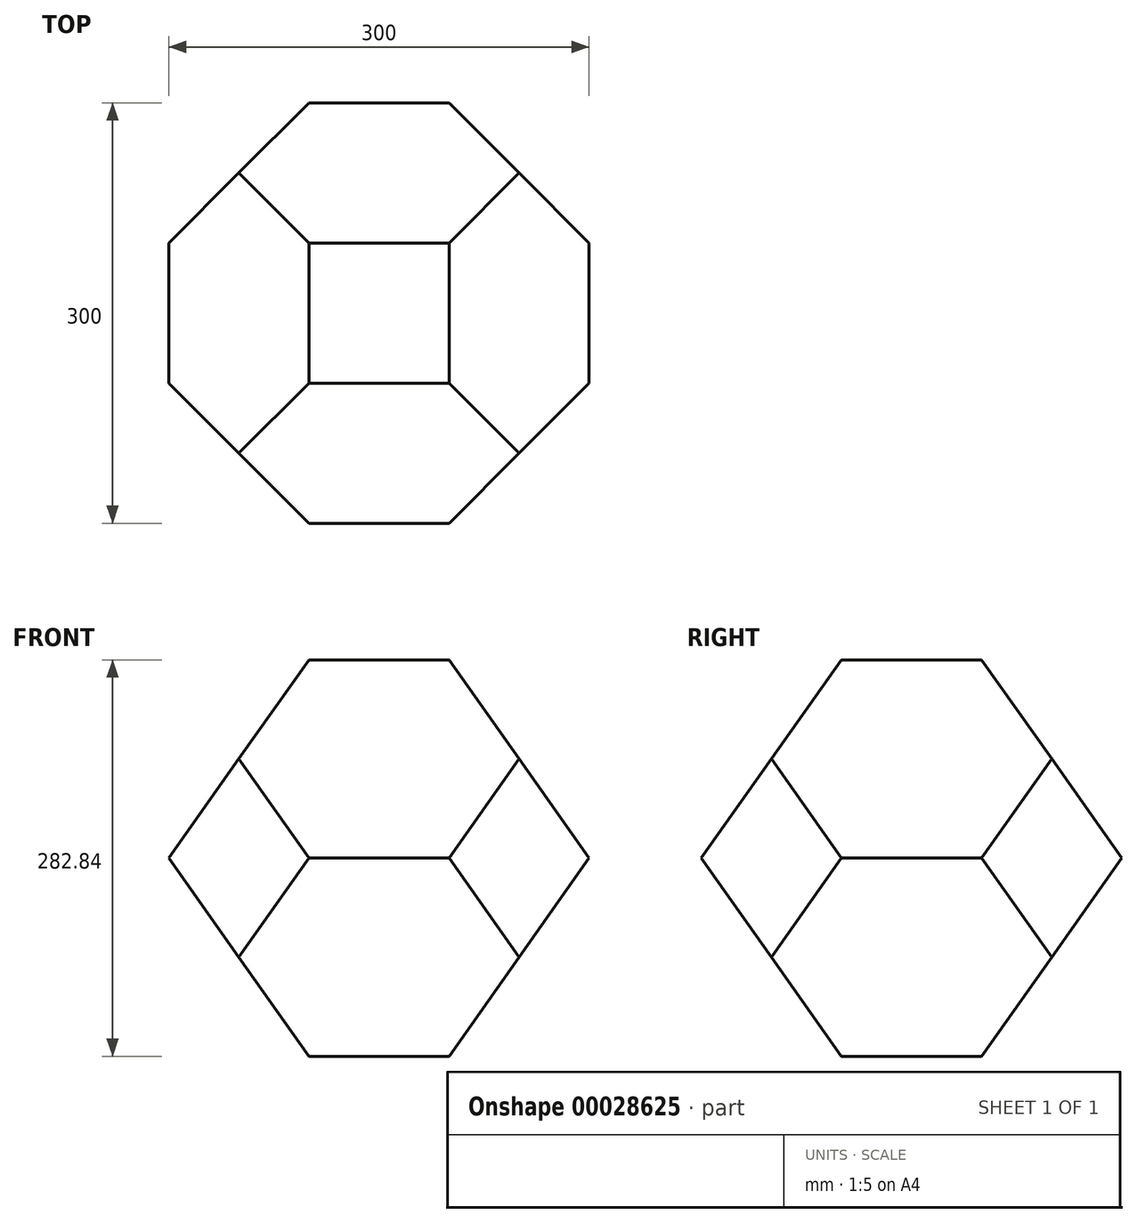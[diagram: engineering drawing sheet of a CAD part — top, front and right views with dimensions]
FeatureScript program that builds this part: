
annotation { "Feature Type Name" : "Feature", "Feature Type Description" : "" }
export const myFeature = defineFeature(function(context is Context, id is Id, definition is map)
    precondition{}
    {
        {
            var Q0;
            Q0=qCreatedBy(makeId("Top.planeOp"),FACE);
            var sketch = newSketch(context, id + "F0", { "sketchPlane" : qUnion([Q0])});
            skCircle(sketch, "E0", {"center": v(0, 0) * mm, "radius": 212.13 * mm});
            skLineSegment(sketch, "E1", {"start": v(-150, -150) * mm, "end": v(150, 150) * mm, "construction": true});
            skLineSegment(sketch, "E2.bottom", {"start": v(-150, -150) * mm, "end": v(150, -150) * mm});
            skLineSegment(sketch, "E2.top", {"start": v(-150, 150) * mm, "end": v(150, 150) * mm});
            skLineSegment(sketch, "E2.left", {"start": v(-150, -150) * mm, "end": v(-150, 150) * mm});
            skLineSegment(sketch, "E2.right", {"start": v(150, -150) * mm, "end": v(150, 150) * mm});
            skSolve(sketch);
        }
        {
            var Q0;
            Q0=qCreatedBy(makeId("Right.planeOp"),FACE);
            var sketch = newSketch(context, id + "F1", { "sketchPlane" : qUnion([Q0])});
            skLineSegment(sketch, "E3", {"start": v(-150, 0) * mm, "end": v(150, 0) * mm});
            skLineSegment(sketch, "E4", {"start": v(150, 0) * mm, "end": v(0, 212.13) * mm});
            skLineSegment(sketch, "E5", {"start": v(0, 212.13) * mm, "end": v(-150, 0) * mm});
            skSolve(sketch);
        }
        {
            var Q0;
            Q0=makeQuery(id+"F1.imprint","IMPRINT",FACE,{"disambiguationData":[TD([[makeQuery(id+"F1.imprint","IMPRINT",EDGE,{"derivedFrom":sQuery(id+"F1.wireOp",EDGE,"E3")}),1.0]])]});
            extrude(context, id + "F2", {"entities" : qUnion([Q0]), "depth" : 150 * mm, "hasSecondDirection" : true, "secondDirectionOppositeDirection" : true, "secondDirectionDepth" : 150 * mm});
        }
        {
            var Q0;
            Q0=qCreatedBy(makeId("Front.planeOp"),FACE);
            var sketch = newSketch(context, id + "F3", { "sketchPlane" : qUnion([Q0])});
            skLineSegment(sketch, "E6", {"start": v(0, 0) * mm, "end": v(0, -178.5) * mm});
            skSolve(sketch);
        }
        {
            var Q0;
            Q0=makeQuery(id+"F2.opExtrude","SWEPT_BODY",BODY,{"disambiguationData":[OSD([sQuery(id+"F1.wireOp",EDGE,"E3"),sQuery(id+"F1.wireOp",EDGE,"E4"),sQuery(id+"F1.wireOp",EDGE,"E5")])]});
            var Q1;
            Q1=sQuery(id+"F3.wireOp",EDGE,"E6");
            transform(context, id + "F4", {"entities" : qUnion([Q0]), "transformType" : TransformType.ROTATION, "transformAxis" : qUnion([Q1]), "angle" : 90 * degree, "makeCopy" : true});
        }
        {
            var Q0;
            Q0=makeQuery(id+"F2.opExtrude","SWEPT_BODY",BODY,{"disambiguationData":[OSD([sQuery(id+"F1.wireOp",EDGE,"E3"),sQuery(id+"F1.wireOp",EDGE,"E4"),sQuery(id+"F1.wireOp",EDGE,"E5")])]});
            var Q1;
            Q1=makeQuery(id+"F4.opPattern","COPY",BODY,{"derivedFrom":makeQuery(id+"F2.opExtrude","SWEPT_BODY",BODY,{"disambiguationData":[OSD([sQuery(id+"F1.wireOp",EDGE,"E3"),sQuery(id+"F1.wireOp",EDGE,"E4"),sQuery(id+"F1.wireOp",EDGE,"E5")])]}),"instanceName":"1"});
            booleanBodies(context, id + "F5", {"operationType" : BooleanOperationType.INTERSECTION, "tools" : qUnion([Q0, Q1])});
        }
        {
            var Q0;
            {var subQ0=makeQuery(id+"F2.opExtrude","SWEPT_BODY",BODY,{"disambiguationData":[OSD([sQuery(id+"F1.wireOp",EDGE,"E3"),sQuery(id+"F1.wireOp",EDGE,"E4"),sQuery(id+"F1.wireOp",EDGE,"E5")])]});Q0=makeQuery(id+"F5.opBoolean","INTERSECT",BODY,{"derivedFrom":[subQ0,makeQuery(id+"F4.opPattern","COPY",BODY,{"derivedFrom":subQ0,"instanceName":"1"})]});}
            var Q1;
            Q1=sQuery(id+"F0.wireOp",EDGE,"E1");
            transform(context, id + "F6", {"entities" : qUnion([Q0]), "transformType" : TransformType.ROTATION, "transformAxis" : qUnion([Q1]), "angle" : 180 * degree, "makeCopy" : true});
        }
        {
            var Q0;
            {var subQ0=makeQuery(id+"F2.opExtrude","SWEPT_BODY",BODY,{"disambiguationData":[OSD([sQuery(id+"F1.wireOp",EDGE,"E3"),sQuery(id+"F1.wireOp",EDGE,"E4"),sQuery(id+"F1.wireOp",EDGE,"E5")])]});Q0=makeQuery(id+"F5.opBoolean","INTERSECT",BODY,{"derivedFrom":[subQ0,makeQuery(id+"F4.opPattern","COPY",BODY,{"derivedFrom":subQ0,"instanceName":"1"})]});}
            var Q1;
            {var subQ0=makeQuery(id+"F2.opExtrude","SWEPT_BODY",BODY,{"disambiguationData":[OSD([sQuery(id+"F1.wireOp",EDGE,"E3"),sQuery(id+"F1.wireOp",EDGE,"E4"),sQuery(id+"F1.wireOp",EDGE,"E5")])]});Q1=makeQuery(id+"F6.opPattern","COPY",BODY,{"derivedFrom":makeQuery(id+"F5.opBoolean","INTERSECT",BODY,{"derivedFrom":[subQ0,makeQuery(id+"F4.opPattern","COPY",BODY,{"derivedFrom":subQ0,"instanceName":"1"})]}),"instanceName":"1"});}
            booleanBodies(context, id + "F7", {"operationType" : BooleanOperationType.UNION, "tools" : qUnion([Q0, Q1])});
        }
        {
            var Q0;
            {var subQ0=makeQuery(id+"F2.opExtrude","SWEPT_FACE",FACE,{"disambiguationData":[OSD([sQuery(id+"F1.wireOp",EDGE,"E4")])]});var subQ1=makeQuery(id+"F2.opExtrude","SWEPT_FACE",FACE,{"disambiguationData":[OSD([sQuery(id+"F1.wireOp",EDGE,"E5")])]});Q0=makeQuery(id+"F5.opBoolean","INTERSECT",VERTEX,{"derivedFrom":[subQ0,subQ1,makeQuery(id+"F4.opPattern","COPY",FACE,{"derivedFrom":subQ0,"instanceName":"1"}),makeQuery(id+"F4.opPattern","COPY",FACE,{"derivedFrom":subQ1,"instanceName":"1"})]});}
            var Q1;
            {var subQ0=sQuery(id+"F1.wireOp",EDGE,"E3");var subQ1=sQuery(id+"F1.wireOp",EDGE,"E5");var subQ2=makeQuery(id+"F5.opBoolean","MERGE",VERTEX,{"derivedFrom":[makeQuery(id+"F2.opExtrude","CAP_VERTEX",VERTEX,{"disambiguationData":[OSD([subQ0,subQ1])],"isStart":true}),makeQuery(id+"F4.opPattern","COPY",VERTEX,{"derivedFrom":makeQuery(id+"F2.opExtrude","CAP_VERTEX",VERTEX,{"disambiguationData":[OSD([subQ0,subQ1])],"isStart":false}),"instanceName":"1"})]});Q1=makeQuery(id+"F7.opBoolean","MERGE",VERTEX,{"derivedFrom":[subQ2,makeQuery(id+"F6.opPattern","COPY",VERTEX,{"derivedFrom":subQ2,"instanceName":"1"})]});}
            var Q2;
            {var subQ0=makeQuery(id+"F2.opExtrude","SWEPT_FACE",FACE,{"disambiguationData":[OSD([sQuery(id+"F1.wireOp",EDGE,"E4")])]});var subQ1=makeQuery(id+"F2.opExtrude","SWEPT_FACE",FACE,{"disambiguationData":[OSD([sQuery(id+"F1.wireOp",EDGE,"E5")])]});Q2=makeQuery(id+"F6.opPattern","COPY",VERTEX,{"derivedFrom":makeQuery(id+"F5.opBoolean","INTERSECT",VERTEX,{"derivedFrom":[subQ0,subQ1,makeQuery(id+"F4.opPattern","COPY",FACE,{"derivedFrom":subQ0,"instanceName":"1"}),makeQuery(id+"F4.opPattern","COPY",FACE,{"derivedFrom":subQ1,"instanceName":"1"})]}),"instanceName":"1"});}
            cPlane(context, id + "F8", {"entities" : qUnion([Q0, Q1, Q2]), "cplaneType" : CPlaneType.THREE_POINT, "offset" : 150 * mm, "width" : 150 * mm, "height" : 150 * mm});
        }
        {
            var Q0;
            Q0=qCreatedBy(id+"F8.planeOp",FACE);
            var sketch = newSketch(context, id + "F9", { "sketchPlane" : qUnion([Q0])});
            skLineSegment(sketch, "E7.0", {"start": v(0, 212.13) * mm, "end": v(212.13, 0) * mm, "construction": true});
            skLineSegment(sketch, "E8", {"start": v(0, 212.13) * mm, "end": v(70.71, 141.42) * mm, "construction": true});
            skLineSegment(sketch, "E9.bottom", {"start": v(132.6, 346.11) * mm, "end": v(-117.64, 346.11) * mm});
            skLineSegment(sketch, "E9.top", {"start": v(132.6, 141.42) * mm, "end": v(-117.64, 141.42) * mm});
            skLineSegment(sketch, "E9.left", {"start": v(132.6, 346.11) * mm, "end": v(132.6, 141.42) * mm});
            skLineSegment(sketch, "E9.right", {"start": v(-117.64, 346.11) * mm, "end": v(-117.64, 141.42) * mm});
            skSolve(sketch);
        }
        {
            var Q0;
            Q0=qCreatedBy(id+"F8.planeOp",FACE);
            var sketch = newSketch(context, id + "F10", { "sketchPlane" : qUnion([Q0])});
            skLineSegment(sketch, "E10", {"start": v(0, 0) * mm, "end": v(-470.52, 0) * mm});
            skLineSegment(sketch, "E11", {"start": v(0, 0) * mm, "end": v(0, -398.6) * mm});
            skSolve(sketch);
        }
        {
            var Q0;
            Q0=makeQuery(id+"F9.imprint","IMPRINT",FACE,{"disambiguationData":[TD([[makeQuery(id+"F9.imprint","IMPRINT",EDGE,{"derivedFrom":sQuery(id+"F9.wireOp",EDGE,"E9.bottom")}),1.0]])]});
            extrude(context, id + "F11", {"entities" : qUnion([Q0]), "depth" : 80 * mm, "hasSecondDirection" : true, "secondDirectionOppositeDirection" : true, "secondDirectionDepth" : 80 * mm});
        }
        {
            var Q0;
            Q0=makeQuery(id+"F11.opExtrude","SWEPT_BODY",BODY,{"disambiguationData":[OSD([sQuery(id+"F9.wireOp",EDGE,"E9.bottom"),sQuery(id+"F9.wireOp",EDGE,"E9.top"),sQuery(id+"F9.wireOp",EDGE,"E9.left"),sQuery(id+"F9.wireOp",EDGE,"E9.right")])]});
            var Q1;
            Q1=sQuery(id+"F10.wireOp",EDGE,"E10");
            circularPattern(context, id + "F12", {"entities" : qUnion([Q0]), "axis" : qUnion([Q1]), "angle" : 90 * degree, "instanceCount" : 4});
        }
        {
            var Q0;
            Q0=makeQuery(id+"F12.opPattern","COPY",BODY,{"derivedFrom":makeQuery(id+"F11.opExtrude","SWEPT_BODY",BODY,{"disambiguationData":[OSD([sQuery(id+"F9.wireOp",EDGE,"E9.bottom"),sQuery(id+"F9.wireOp",EDGE,"E9.top"),sQuery(id+"F9.wireOp",EDGE,"E9.left"),sQuery(id+"F9.wireOp",EDGE,"E9.right")])]}),"instanceName":"3"});
            var Q1;
            Q1=makeQuery(id+"F12.opPattern","COPY",BODY,{"derivedFrom":makeQuery(id+"F11.opExtrude","SWEPT_BODY",BODY,{"disambiguationData":[OSD([sQuery(id+"F9.wireOp",EDGE,"E9.bottom"),sQuery(id+"F9.wireOp",EDGE,"E9.top"),sQuery(id+"F9.wireOp",EDGE,"E9.left"),sQuery(id+"F9.wireOp",EDGE,"E9.right")])]}),"instanceName":"1"});
            var Q2;
            Q2=sQuery(id+"F10.wireOp",EDGE,"E11");
            circularPattern(context, id + "F13", {"entities" : qUnion([Q0, Q1]), "axis" : qUnion([Q2]), "angle" : 90 * degree, "instanceCount" : 2});
        }
        {
            var Q0;
            Q0=makeQuery(id+"F11.opExtrude","SWEPT_BODY",BODY,{"disambiguationData":[OSD([sQuery(id+"F9.wireOp",EDGE,"E9.bottom"),sQuery(id+"F9.wireOp",EDGE,"E9.top"),sQuery(id+"F9.wireOp",EDGE,"E9.left"),sQuery(id+"F9.wireOp",EDGE,"E9.right")])]});
            var Q1;
            Q1=makeQuery(id+"F12.opPattern","COPY",BODY,{"derivedFrom":makeQuery(id+"F11.opExtrude","SWEPT_BODY",BODY,{"disambiguationData":[OSD([sQuery(id+"F9.wireOp",EDGE,"E9.bottom"),sQuery(id+"F9.wireOp",EDGE,"E9.top"),sQuery(id+"F9.wireOp",EDGE,"E9.left"),sQuery(id+"F9.wireOp",EDGE,"E9.right")])]}),"instanceName":"3"});
            var Q2;
            Q2=makeQuery(id+"F13.opPattern","COPY",BODY,{"derivedFrom":makeQuery(id+"F12.opPattern","COPY",BODY,{"derivedFrom":makeQuery(id+"F11.opExtrude","SWEPT_BODY",BODY,{"disambiguationData":[OSD([sQuery(id+"F9.wireOp",EDGE,"E9.bottom"),sQuery(id+"F9.wireOp",EDGE,"E9.top"),sQuery(id+"F9.wireOp",EDGE,"E9.left"),sQuery(id+"F9.wireOp",EDGE,"E9.right")])]}),"instanceName":"3"}),"instanceName":"1"});
            var Q3;
            Q3=makeQuery(id+"F12.opPattern","COPY",BODY,{"derivedFrom":makeQuery(id+"F11.opExtrude","SWEPT_BODY",BODY,{"disambiguationData":[OSD([sQuery(id+"F9.wireOp",EDGE,"E9.bottom"),sQuery(id+"F9.wireOp",EDGE,"E9.top"),sQuery(id+"F9.wireOp",EDGE,"E9.left"),sQuery(id+"F9.wireOp",EDGE,"E9.right")])]}),"instanceName":"2"});
            var Q4;
            Q4=makeQuery(id+"F12.opPattern","COPY",BODY,{"derivedFrom":makeQuery(id+"F11.opExtrude","SWEPT_BODY",BODY,{"disambiguationData":[OSD([sQuery(id+"F9.wireOp",EDGE,"E9.bottom"),sQuery(id+"F9.wireOp",EDGE,"E9.top"),sQuery(id+"F9.wireOp",EDGE,"E9.left"),sQuery(id+"F9.wireOp",EDGE,"E9.right")])]}),"instanceName":"1"});
            var Q5;
            Q5=makeQuery(id+"F13.opPattern","COPY",BODY,{"derivedFrom":makeQuery(id+"F12.opPattern","COPY",BODY,{"derivedFrom":makeQuery(id+"F11.opExtrude","SWEPT_BODY",BODY,{"disambiguationData":[OSD([sQuery(id+"F9.wireOp",EDGE,"E9.bottom"),sQuery(id+"F9.wireOp",EDGE,"E9.top"),sQuery(id+"F9.wireOp",EDGE,"E9.left"),sQuery(id+"F9.wireOp",EDGE,"E9.right")])]}),"instanceName":"1"}),"instanceName":"1"});
            var Q6;
            {var subQ0=makeQuery(id+"F2.opExtrude","SWEPT_BODY",BODY,{"disambiguationData":[OSD([sQuery(id+"F1.wireOp",EDGE,"E3"),sQuery(id+"F1.wireOp",EDGE,"E4"),sQuery(id+"F1.wireOp",EDGE,"E5")])]});Q6=makeQuery(id+"F5.opBoolean","INTERSECT",BODY,{"derivedFrom":[subQ0,makeQuery(id+"F4.opPattern","COPY",BODY,{"derivedFrom":subQ0,"instanceName":"1"})]});}
            booleanBodies(context, id + "F14", {"operationType" : BooleanOperationType.SUBTRACTION, "tools" : qUnion([Q0, Q1, Q2, Q3, Q4, Q5]), "targets" : qUnion([Q6])});
        }
    });
